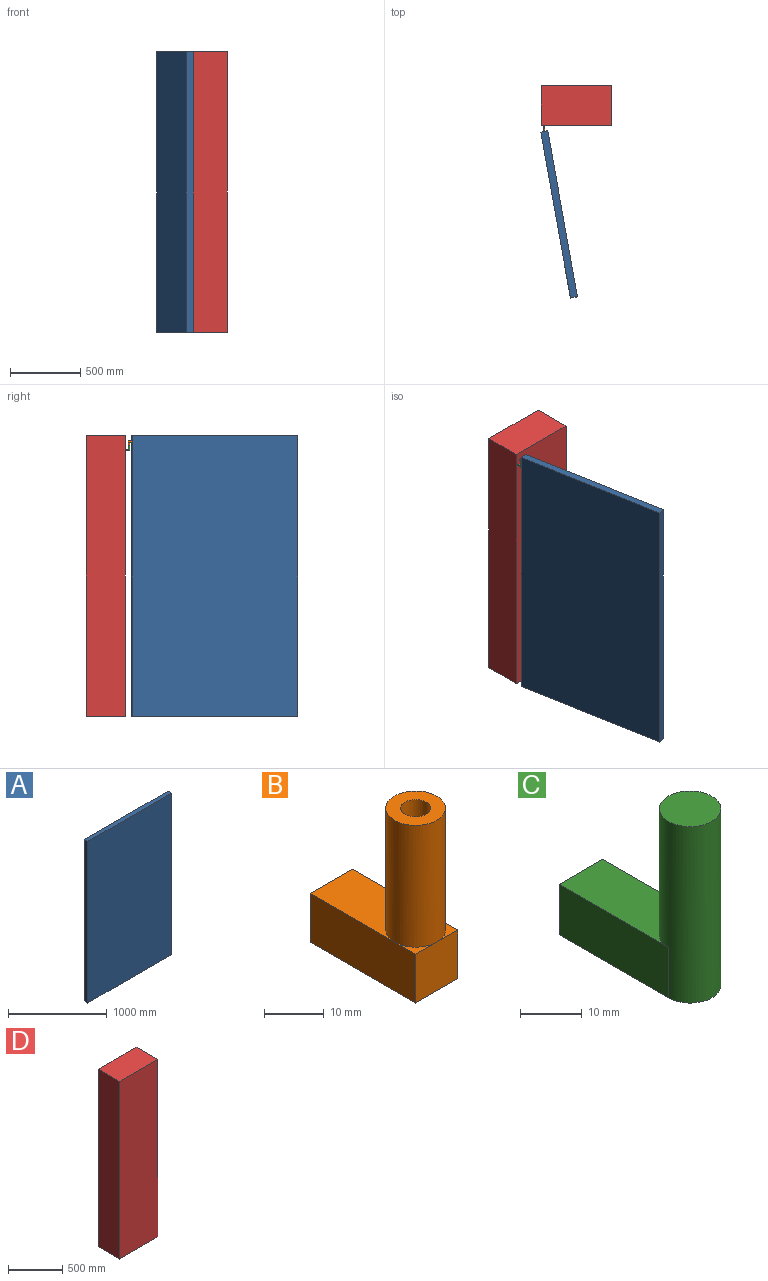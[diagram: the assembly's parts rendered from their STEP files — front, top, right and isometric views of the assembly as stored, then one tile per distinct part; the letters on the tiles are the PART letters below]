
ASSEMBLY  parts=4 mates=3
PART A: 6 faces, bbox 1200x50x2000 mm
  f0: plane 2000x1200mm, normal (0,1,0), area 2400000mm2, adj f1,f3,f4,f5
  f1: plane 2000x50mm, normal (-1,0,0), area 100000mm2, adj f0,f2,f4,f5
  f2: plane 2000x1200mm, normal (0,-1,0), area 2400000mm2, adj f1,f3,f4,f5
  f3: plane 2000x50mm, normal (1,0,0), area 100000mm2, adj f0,f2,f4,f5
  f4: plane 1200x50mm, normal (0,0,1), area 60000mm2, adj f0,f1,f2,f3
  f5: plane 1200x50mm, normal (0,0,-1), area 60000mm2, adj f0,f1,f2,f3
PART B: 12 faces, bbox 10x25x35 mm
  f0: plane 20x10mm, normal (0,0,1), area 160.7mm2, adj f3,f5,f7,f9
  f1: plane 5x5mm, normal (0,0,1), area 5.4mm2, adj f5,f6,f9
  f2: plane 25x10mm, normal (0,0,-1), area 250mm2, adj f3,f5,f6,f7
  f3: plane 25x10mm, normal (1,0,0), area 250mm2, adj f0,f2,f4,f6,f7
  f4: plane 5x5mm, normal (0,0,1), area 5.4mm2, adj f3,f6,f9
  f5: plane 25x10mm, normal (-1,0,0), area 250mm2, adj f0,f1,f2,f6,f7
  f6: plane 10x10mm, normal (0,-1,0), area 100mm2, adj f1,f2,f3,f4,f5
  f7: plane 10x10mm, normal (0,1,0), area 100mm2, adj f0,f2,f3,f5
  f8: cylinder r=2.5mm len=25mm, axis (0,0,-1), area 392.7mm2, adj f10,f11
  f9: cylinder r=5mm len=25mm, axis (0,0,-1), area 785.4mm2, adj f0,f1,f4,f10
  f10: plane 10x10mm, normal (0,0,1), area 58.9mm2, adj f8,f9
  f11: plane 5x5mm, normal (0,0,1), area 19.6mm2, adj f8
PART C: 7 faces, bbox 10x30x35 mm
  f0: plane 30x10mm, normal (0,0,-1), area 289.3mm2, adj f1,f2,f4,f5
  f1: plane 25x10mm, normal (1,0,0), area 250mm2, adj f0,f3,f4,f5
  f2: plane 25x10mm, normal (-1,0,0), area 250mm2, adj f0,f3,f4,f5
  f3: plane 25x10mm, normal (0,0,1), area 210.7mm2, adj f1,f2,f4,f5
  f4: plane 10x10mm, normal (0,1,0), area 100mm2, adj f0,f1,f2,f3
  f5: cylinder r=5mm len=35mm, axis (0,0,-1), area 942.5mm2, adj f0,f1,f2,f3,f6
  f6: plane 10x10mm, normal (0,0,1), area 78.5mm2, adj f5
PART D: 6 faces, bbox 500x280x2000 mm
  f0: plane 2000x280mm, normal (-1,0,0), area 560000mm2, adj f1,f3,f4,f5
  f1: plane 500x280mm, normal (0,0,-1), area 140000mm2, adj f0,f2,f4,f5
  f2: plane 2000x280mm, normal (1,0,0), area 560000mm2, adj f1,f3,f4,f5
  f3: plane 500x280mm, normal (0,0,1), area 140000mm2, adj f0,f2,f4,f5
  f4: plane 2000x500mm, normal (0,-1,0), area 1000000mm2, adj f0,f1,f2,f3
  f5: plane 2000x500mm, normal (0,1,0), area 1000000mm2, adj f0,f1,f2,f3
PLACE A rot(axis=(0,0,1),100.1deg) t=(210.07,-1510.36,0)mm
PLACE B rot(axis=(-1,-0.09,0),180deg) t=(23.52,-324.69,1960)mm
PLACE C t=(20,-280,1900)mm
PLACE D at identity fixed
MATE revolute C.f5 <-> B.f8  axis (0,0,1) through (20,-305,1930)mm
MATE fastened B.f7 <-> A.f3  axis (0.18,-0.98,0) through (23.52,-324.69,1960)mm
MATE fastened D.f4 <-> C.f4  axis (0,1,0) through (20,-280,1900)mm
